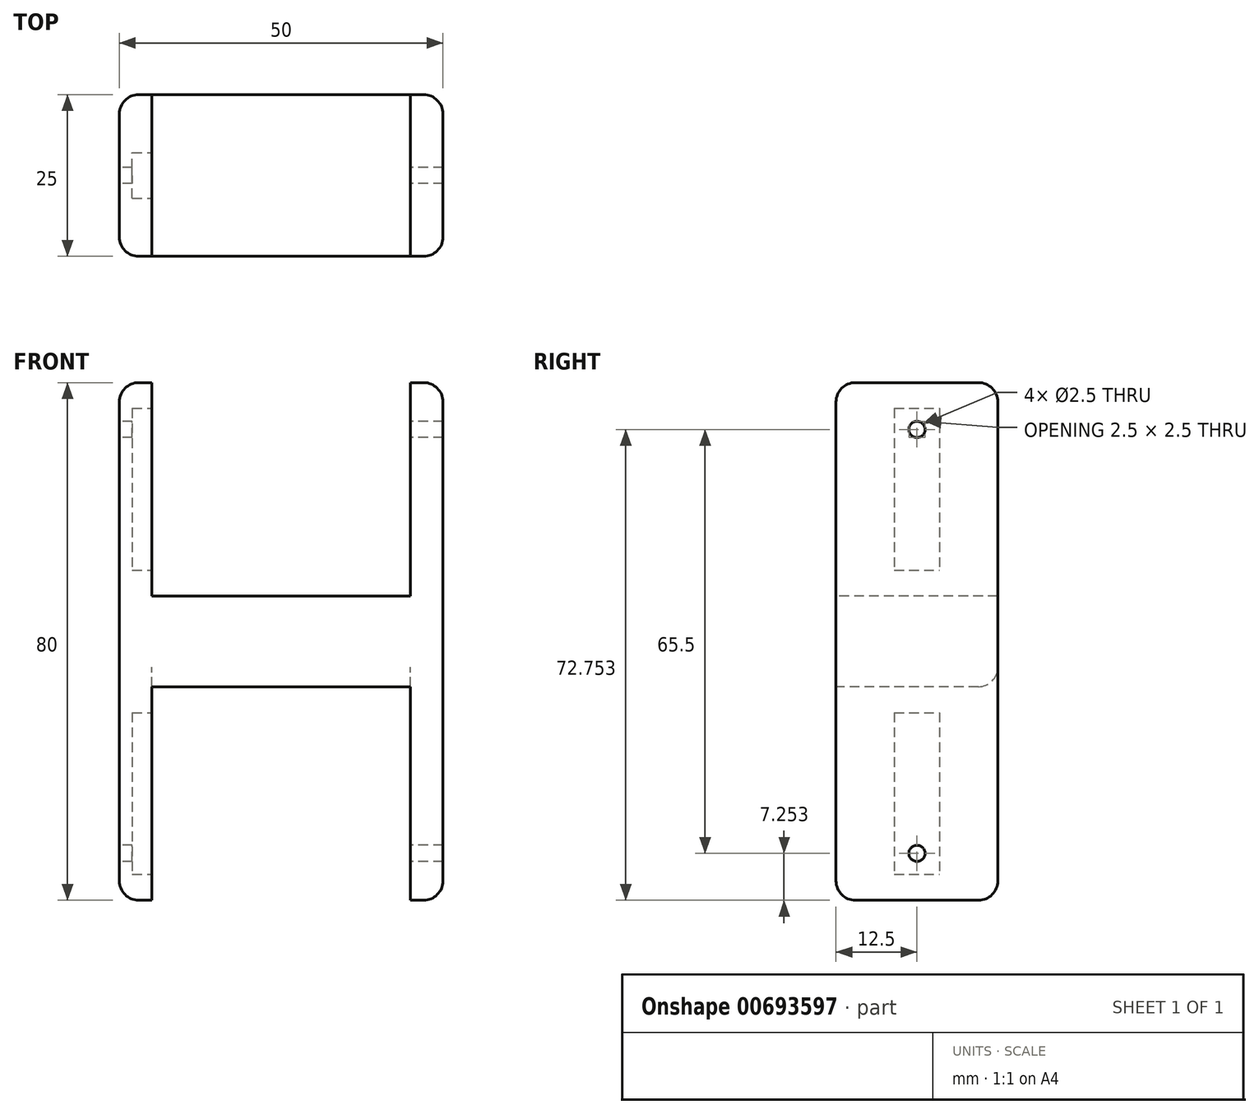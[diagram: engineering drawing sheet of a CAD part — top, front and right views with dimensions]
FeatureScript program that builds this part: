
annotation { "Feature Type Name" : "Feature", "Feature Type Description" : "" }
export const myFeature = defineFeature(function(context is Context, id is Id, definition is map)
    precondition{}
    {
        {
            var Q0;
            Q0=qCreatedBy(makeId("Front.planeOp"),FACE);
            var sketch = newSketch(context, id + "F0", { "sketchPlane" : qUnion([Q0])});
            skLineSegment(sketch, "E0.bottom", {"start": v(-21, 65.16) * mm, "end": v(29, 65.16) * mm});
            skLineSegment(sketch, "E0.top", {"start": v(-21, -14.84) * mm, "end": v(29, -14.84) * mm});
            skLineSegment(sketch, "E0.left", {"start": v(-21, 65.16) * mm, "end": v(-21, -14.84) * mm});
            skLineSegment(sketch, "E0.right", {"start": v(29, 65.16) * mm, "end": v(29, -14.84) * mm});
            skSolve(sketch);
        }
        {
            var Q0;
            Q0=qSketchRegion(id+"F0",true);
            extrude(context, id + "F1", {"entities" : qUnion([Q0]), "depth" : 25 * mm, "offsetDistance" : 25 * mm});
        }
        {
            var Q0;
            Q0=makeQuery(id+"F1.opExtrude","CAP_FACE",FACE,{"disambiguationData":[OSD([sQuery(id+"F0.wireOp",EDGE,"E0.bottom"),sQuery(id+"F0.wireOp",EDGE,"E0.top"),sQuery(id+"F0.wireOp",EDGE,"E0.left"),sQuery(id+"F0.wireOp",EDGE,"E0.right")])],"isStart":false});
            var sketch = newSketch(context, id + "F2", { "sketchPlane" : qUnion([Q0])});
            skLineSegment(sketch, "E1.bottom", {"start": v(24, -14.84) * mm, "end": v(-16, -14.84) * mm});
            skLineSegment(sketch, "E1.top", {"start": v(24, 18.16) * mm, "end": v(-16, 18.16) * mm});
            skLineSegment(sketch, "E1.left", {"start": v(24, -14.84) * mm, "end": v(24, 18.16) * mm});
            skLineSegment(sketch, "E1.right", {"start": v(-16, -14.84) * mm, "end": v(-16, 18.16) * mm});
            skLineSegment(sketch, "E2.bottom", {"start": v(-16, 65.16) * mm, "end": v(24, 65.16) * mm});
            skLineSegment(sketch, "E2.top", {"start": v(-16, 32.16) * mm, "end": v(24, 32.16) * mm});
            skLineSegment(sketch, "E2.left", {"start": v(-16, 65.16) * mm, "end": v(-16, 32.16) * mm});
            skLineSegment(sketch, "E2.right", {"start": v(24, 65.16) * mm, "end": v(24, 32.16) * mm});
            skSolve(sketch);
        }
        {
            var Q0;
            Q0=qSketchRegion(id+"F2",true);
            extrude(context, id + "F3", {"entities" : qUnion([Q0]), "operationType" : NewBodyOperationType.REMOVE, "endBound" : BoundingType.THROUGH_ALL, "oppositeDirection" : true, "depth" : 25 * mm, "offsetDistance" : 25 * mm});
        }
        {
            var Q0;
            Q0=makeQuery(id+"F3.boolean.opBoolean","COPY",FACE,{"derivedFrom":makeQuery(id+"F3.opExtrude","SWEPT_FACE",FACE,{"disambiguationData":[OSD([sQuery(id+"F2.wireOp",EDGE,"E1.right")])]})});
            var sketch = newSketch(context, id + "F4", { "sketchPlane" : qUnion([Q0])});
            skLineSegment(sketch, "E3.bottom", {"start": v(-16, 14.16) * mm, "end": v(-9, 14.16) * mm});
            skLineSegment(sketch, "E3.top", {"start": v(-16, -10.84) * mm, "end": v(-9, -10.84) * mm});
            skLineSegment(sketch, "E3.left", {"start": v(-16, 14.16) * mm, "end": v(-16, -10.84) * mm});
            skLineSegment(sketch, "E3.right", {"start": v(-9, 14.16) * mm, "end": v(-9, -10.84) * mm});
            skLineSegment(sketch, "E4.bottom", {"start": v(-16, 61.16) * mm, "end": v(-9, 61.16) * mm});
            skLineSegment(sketch, "E4.top", {"start": v(-16, 36.16) * mm, "end": v(-9, 36.16) * mm});
            skLineSegment(sketch, "E4.left", {"start": v(-16, 61.16) * mm, "end": v(-16, 36.16) * mm});
            skLineSegment(sketch, "E4.right", {"start": v(-9, 61.16) * mm, "end": v(-9, 36.16) * mm});
            skSolve(sketch);
        }
        {
            var Q0;
            Q0=qSketchRegion(id+"F4",true);
            extrude(context, id + "F5", {"entities" : qUnion([Q0]), "operationType" : NewBodyOperationType.REMOVE, "oppositeDirection" : true, "depth" : 3 * mm, "offsetDistance" : 25 * mm});
        }
        {
            var Q0;
            Q0=makeQuery(id+"F1.opExtrude","SWEPT_FACE",FACE,{"disambiguationData":[OSD([sQuery(id+"F0.wireOp",EDGE,"E0.left")])]});
            var sketch = newSketch(context, id + "F6", { "sketchPlane" : qUnion([Q0])});
            skCircle(sketch, "E5", {"center": v(12.5, -7.59) * mm, "radius": 1.25 * mm});
            skCircle(sketch, "E6", {"center": v(12.5, 57.91) * mm, "radius": 1.25 * mm});
            skSolve(sketch);
        }
        {
            var Q0;
            Q0=qSketchRegion(id+"F6",true);
            extrude(context, id + "F7", {"entities" : qUnion([Q0]), "operationType" : NewBodyOperationType.REMOVE, "endBound" : BoundingType.THROUGH_ALL, "oppositeDirection" : true, "depth" : 25 * mm, "offsetDistance" : 25 * mm});
        }
        {
            var Q0;
            Q0=makeQuery(id+"F1.opExtrude","SWEPT_EDGE",EDGE,{"disambiguationData":[OSD([sQuery(id+"F0.wireOp",EDGE,"E0.bottom"),sQuery(id+"F0.wireOp",EDGE,"E0.right")])]});
            var Q1;
            Q1=makeQuery(id+"F1.opExtrude","SWEPT_EDGE",EDGE,{"disambiguationData":[OSD([sQuery(id+"F0.wireOp",EDGE,"E0.bottom"),sQuery(id+"F0.wireOp",EDGE,"E0.left")])]});
            var Q2;
            Q2=makeQuery(id+"F1.opExtrude","CAP_EDGE",EDGE,{"disambiguationData":[OSD([sQuery(id+"F0.wireOp",EDGE,"E0.bottom")])],"isStart":true});
            var Q3;
            Q3=makeQuery(id+"F1.opExtrude","CAP_EDGE",EDGE,{"disambiguationData":[OSD([sQuery(id+"F0.wireOp",EDGE,"E0.bottom")])],"isStart":false});
            var Q4;
            Q4=makeQuery(id+"F1.opExtrude","CAP_EDGE",EDGE,{"disambiguationData":[OSD([sQuery(id+"F0.wireOp",EDGE,"E0.right")])],"isStart":false});
            var Q5;
            Q5=makeQuery(id+"F1.opExtrude","CAP_EDGE",EDGE,{"disambiguationData":[OSD([sQuery(id+"F0.wireOp",EDGE,"E0.right")])],"isStart":true});
            var Q6;
            Q6=makeQuery(id+"F1.opExtrude","CAP_EDGE",EDGE,{"disambiguationData":[OSD([sQuery(id+"F0.wireOp",EDGE,"E0.left")])],"isStart":false});
            var Q7;
            Q7=makeQuery(id+"F1.opExtrude","CAP_EDGE",EDGE,{"disambiguationData":[OSD([sQuery(id+"F0.wireOp",EDGE,"E0.left")])],"isStart":true});
            var Q8;
            Q8=makeQuery(id+"F1.opExtrude","SWEPT_EDGE",EDGE,{"disambiguationData":[OSD([sQuery(id+"F0.wireOp",EDGE,"E0.top"),sQuery(id+"F0.wireOp",EDGE,"E0.left")])]});
            var Q9;
            Q9=makeQuery(id+"F1.opExtrude","SWEPT_EDGE",EDGE,{"disambiguationData":[OSD([sQuery(id+"F0.wireOp",EDGE,"E0.top"),sQuery(id+"F0.wireOp",EDGE,"E0.right")])]});
            var Q10;
            {var subQ0=sQuery(id+"F0.wireOp",EDGE,"E0.left");var subQ1=sQuery(id+"F0.wireOp",EDGE,"E0.top");Q10=makeQuery(id+"F3.boolean.opBoolean","SPLIT",EDGE,{"disambiguationData":[TD([makeQuery(id+"F1.opExtrude","SWEPT_FACE",FACE,{"disambiguationData":[OSD([subQ0])]})])],"derivedFrom":makeQuery(id+"F1.opExtrude","CAP_EDGE",EDGE,{"disambiguationData":[OSD([subQ1])],"isStart":false})});}
            var Q11;
            {var subQ0=sQuery(id+"F0.wireOp",EDGE,"E0.left");var subQ1=sQuery(id+"F0.wireOp",EDGE,"E0.top");Q11=makeQuery(id+"F3.boolean.opBoolean","SPLIT",EDGE,{"disambiguationData":[TD([makeQuery(id+"F1.opExtrude","SWEPT_FACE",FACE,{"disambiguationData":[OSD([subQ0])]})])],"derivedFrom":makeQuery(id+"F1.opExtrude","CAP_EDGE",EDGE,{"disambiguationData":[OSD([subQ1])],"isStart":true})});}
            var Q12;
            {var subQ0=sQuery(id+"F0.wireOp",EDGE,"E0.right");var subQ1=sQuery(id+"F0.wireOp",EDGE,"E0.top");Q12=makeQuery(id+"F3.boolean.opBoolean","SPLIT",EDGE,{"disambiguationData":[TD([makeQuery(id+"F1.opExtrude","SWEPT_FACE",FACE,{"disambiguationData":[OSD([subQ0])]})])],"derivedFrom":makeQuery(id+"F1.opExtrude","CAP_EDGE",EDGE,{"disambiguationData":[OSD([subQ1])],"isStart":true})});}
            var Q13;
            {var subQ0=sQuery(id+"F0.wireOp",EDGE,"E0.right");var subQ1=sQuery(id+"F0.wireOp",EDGE,"E0.top");Q13=makeQuery(id+"F3.boolean.opBoolean","SPLIT",EDGE,{"disambiguationData":[TD([makeQuery(id+"F1.opExtrude","SWEPT_FACE",FACE,{"disambiguationData":[OSD([subQ0])]})])],"derivedFrom":makeQuery(id+"F1.opExtrude","CAP_EDGE",EDGE,{"disambiguationData":[OSD([subQ1])],"isStart":false})});}
            var Q14;
            Q14=makeQuery(id+"F3.boolean.opBoolean","COPY",EDGE,{"derivedFrom":makeQuery(id+"F3.opExtrude","CAP_EDGE",EDGE,{"disambiguationData":[OSD([sQuery(id+"F2.wireOp",EDGE,"E1.top")])],"isStart":true})});
            var Q15;
            Q15=makeQuery(id+"F3.boolean.opBoolean","INTERSECT",EDGE,{"derivedFrom":[makeQuery(id+"F1.opExtrude","CAP_FACE",FACE,{"disambiguationData":[OSD([sQuery(id+"F0.wireOp",EDGE,"E0.bottom"),sQuery(id+"F0.wireOp",EDGE,"E0.top"),sQuery(id+"F0.wireOp",EDGE,"E0.left"),sQuery(id+"F0.wireOp",EDGE,"E0.right")])],"isStart":true}),makeQuery(id+"F3.opExtrude","SWEPT_FACE",FACE,{"disambiguationData":[OSD([sQuery(id+"F2.wireOp",EDGE,"E1.top")])]})]});
            fillet(context, id + "F8", {"entities" : qUnion([Q0, Q1, Q2, Q3, Q4, Q5, Q6, Q7, Q8, Q9, Q10, Q11, Q12, Q13, Q14, Q15]), "radius" : 3 * mm, "tangentPropagation" : true, "allowEdgeOverflow" : false});
        }
    });
